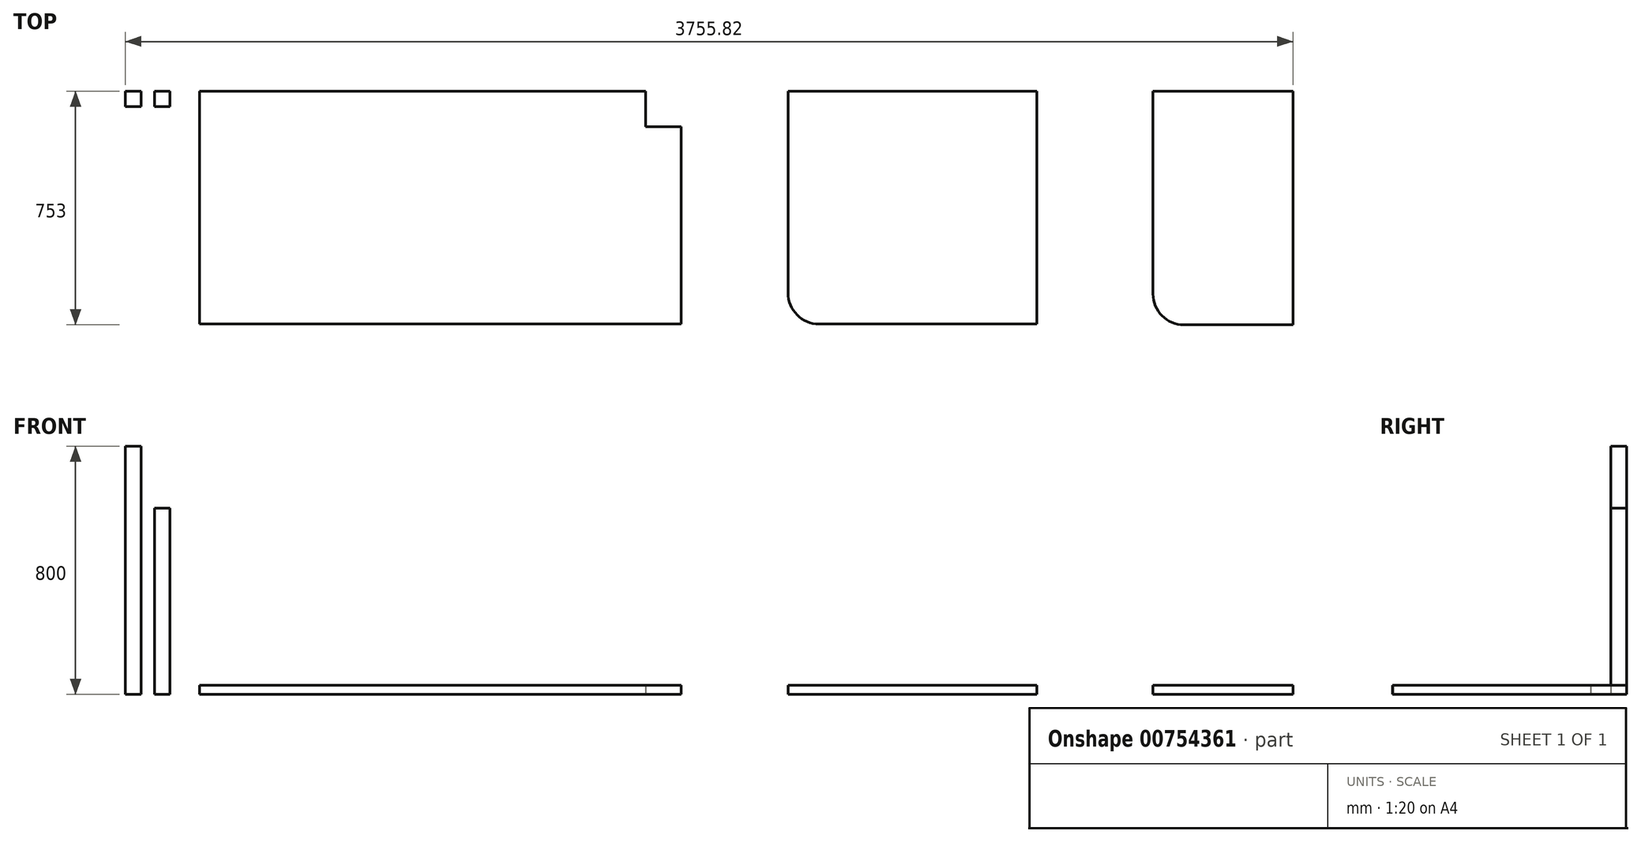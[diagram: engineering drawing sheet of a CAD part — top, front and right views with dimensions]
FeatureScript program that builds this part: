
annotation { "Feature Type Name" : "Feature", "Feature Type Description" : "" }
export const myFeature = defineFeature(function(context is Context, id is Id, definition is map)
    precondition{}
    {
        {
            var Q0;
            Q0=qCreatedBy(makeId("Top.planeOp"),FACE);
            var sketch = newSketch(context, id + "F0", { "sketchPlane" : qUnion([Q0])});
            skLineSegment(sketch, "E0.bottom", {"start": v(0, 0) * mm, "end": v(-1550, 0) * mm});
            skLineSegment(sketch, "E0.top", {"start": v(0, -750) * mm, "end": v(-1550, -750) * mm});
            skLineSegment(sketch, "E0.left", {"start": v(0, 0) * mm, "end": v(0, -750) * mm});
            skLineSegment(sketch, "E0.right", {"start": v(-1550, 0) * mm, "end": v(-1550, -750) * mm});
            skPoint(sketch, "E1", {"position": v(-115, -115) * mm});
            skLineSegment(sketch, "E2", {"start": v(-115, -115) * mm, "end": v(0, -115) * mm});
            skLineSegment(sketch, "E3", {"start": v(-115, -115) * mm, "end": v(-115, 0) * mm});
            skSolve(sketch);
        }
        {
            var Q0;
            Q0=qCreatedBy(makeId("Top.planeOp"),FACE);
            var sketch = newSketch(context, id + "F1", { "sketchPlane" : qUnion([Q0])});
            skLineSegment(sketch, "E4.bottom", {"start": v(343.12, 0) * mm, "end": v(1143.12, 0) * mm});
            skLineSegment(sketch, "E4.top", {"start": v(343.12, -750) * mm, "end": v(1143.12, -750) * mm});
            skLineSegment(sketch, "E4.left", {"start": v(343.12, 0) * mm, "end": v(343.12, -750) * mm});
            skLineSegment(sketch, "E4.right", {"start": v(1143.12, 0) * mm, "end": v(1143.12, -750) * mm});
            skSolve(sketch);
        }
        {
            var Q0;
            Q0=makeQuery(id+"F1.imprint","IMPRINT",FACE,{"disambiguationData":[TD([[makeQuery(id+"F1.imprint","IMPRINT",EDGE,{"derivedFrom":sQuery(id+"F1.wireOp",EDGE,"E4.bottom")}),-1.0]])]});
            var Q1;
            {var subQ2=sQuery(id+"F0.wireOp",EDGE,"E0.top");Q1=makeQuery(id+"F0.imprint","IMPRINT",FACE,{"disambiguationData":[TD([[makeQuery(id+"F0.imprint","IMPRINT",EDGE,{"derivedFrom":subQ2}),-1.0]])]});}
            extrude(context, id + "F2", {"entities" : qUnion([Q0, Q1]), "depth" : 30 * mm, "offsetDistance" : 25 * mm});
        }
        {
            var Q0;
            Q0=makeQuery(id+"F2.opExtrude","SWEPT_EDGE",EDGE,{"disambiguationData":[OSD([sQuery(id+"F1.wireOp",EDGE,"E4.top"),sQuery(id+"F1.wireOp",EDGE,"E4.left")])]});
            fillet(context, id + "F3", {"entities" : qUnion([Q0]), "radius" : 100 * mm, "tangentPropagation" : true, "allowEdgeOverflow" : false});
        }
        {
            var Q0;
            Q0=qCreatedBy(makeId("Top.planeOp"),FACE);
            var sketch = newSketch(context, id + "F4", { "sketchPlane" : qUnion([Q0])});
            skLineSegment(sketch, "E5.bottom", {"start": v(-1738.33, 0) * mm, "end": v(-1788.33, 0) * mm});
            skLineSegment(sketch, "E5.top", {"start": v(-1738.33, -50) * mm, "end": v(-1788.33, -50) * mm});
            skLineSegment(sketch, "E5.left", {"start": v(-1738.33, 0) * mm, "end": v(-1738.33, -50) * mm});
            skLineSegment(sketch, "E5.right", {"start": v(-1788.33, 0) * mm, "end": v(-1788.33, -50) * mm});
            skSolve(sketch);
        }
        {
            var Q0;
            Q0=makeQuery(id+"F4.imprint","IMPRINT",FACE,{"disambiguationData":[TD([[makeQuery(id+"F4.imprint","IMPRINT",EDGE,{"derivedFrom":sQuery(id+"F4.wireOp",EDGE,"E5.bottom")}),1.0]])]});
            extrude(context, id + "F5", {"entities" : qUnion([Q0]), "depth" : 800 * mm, "offsetDistance" : 25 * mm});
        }
        {
            var Q0;
            Q0=qCreatedBy(makeId("Top.planeOp"),FACE);
            var sketch = newSketch(context, id + "F6", { "sketchPlane" : qUnion([Q0])});
            skLineSegment(sketch, "E6.bottom", {"start": v(-1645.27, 0) * mm, "end": v(-1695.27, 0) * mm});
            skLineSegment(sketch, "E6.top", {"start": v(-1645.27, -50) * mm, "end": v(-1695.27, -50) * mm});
            skLineSegment(sketch, "E6.left", {"start": v(-1645.27, 0) * mm, "end": v(-1645.27, -50) * mm});
            skLineSegment(sketch, "E6.right", {"start": v(-1695.27, 0) * mm, "end": v(-1695.27, -50) * mm});
            skSolve(sketch);
        }
        {
            var Q0;
            Q0=makeQuery(id+"F6.imprint","IMPRINT",FACE,{"disambiguationData":[TD([[makeQuery(id+"F6.imprint","IMPRINT",EDGE,{"derivedFrom":sQuery(id+"F6.wireOp",EDGE,"E6.bottom")}),1.0]])]});
            extrude(context, id + "F7", {"entities" : qUnion([Q0]), "depth" : 600 * mm, "offsetDistance" : 25 * mm});
        }
        {
            var Q0;
            Q0=qCreatedBy(makeId("Top.planeOp"),FACE);
            var sketch = newSketch(context, id + "F8", { "sketchPlane" : qUnion([Q0])});
            skLineSegment(sketch, "E7.bottom", {"start": v(1517.49, 0) * mm, "end": v(1967.49, 0) * mm});
            skLineSegment(sketch, "E7.top", {"start": v(1517.49, -753) * mm, "end": v(1967.49, -753) * mm});
            skLineSegment(sketch, "E7.left", {"start": v(1517.49, 0) * mm, "end": v(1517.49, -753) * mm});
            skLineSegment(sketch, "E7.right", {"start": v(1967.49, 0) * mm, "end": v(1967.49, -753) * mm});
            skSolve(sketch);
        }
        {
            var Q0;
            Q0=makeQuery(id+"F8.imprint","IMPRINT",FACE,{"disambiguationData":[TD([[makeQuery(id+"F8.imprint","IMPRINT",EDGE,{"derivedFrom":sQuery(id+"F8.wireOp",EDGE,"E7.bottom")}),-1.0]])]});
            extrude(context, id + "F9", {"entities" : qUnion([Q0]), "depth" : 30 * mm, "offsetDistance" : 25 * mm});
        }
        {
            var Q0;
            Q0=makeQuery(id+"F9.opExtrude","SWEPT_EDGE",EDGE,{"disambiguationData":[OSD([sQuery(id+"F8.wireOp",EDGE,"E7.top"),sQuery(id+"F8.wireOp",EDGE,"E7.left")])]});
            fillet(context, id + "F10", {"entities" : qUnion([Q0]), "radius" : 100 * mm, "tangentPropagation" : true, "allowEdgeOverflow" : false});
        }
    });
